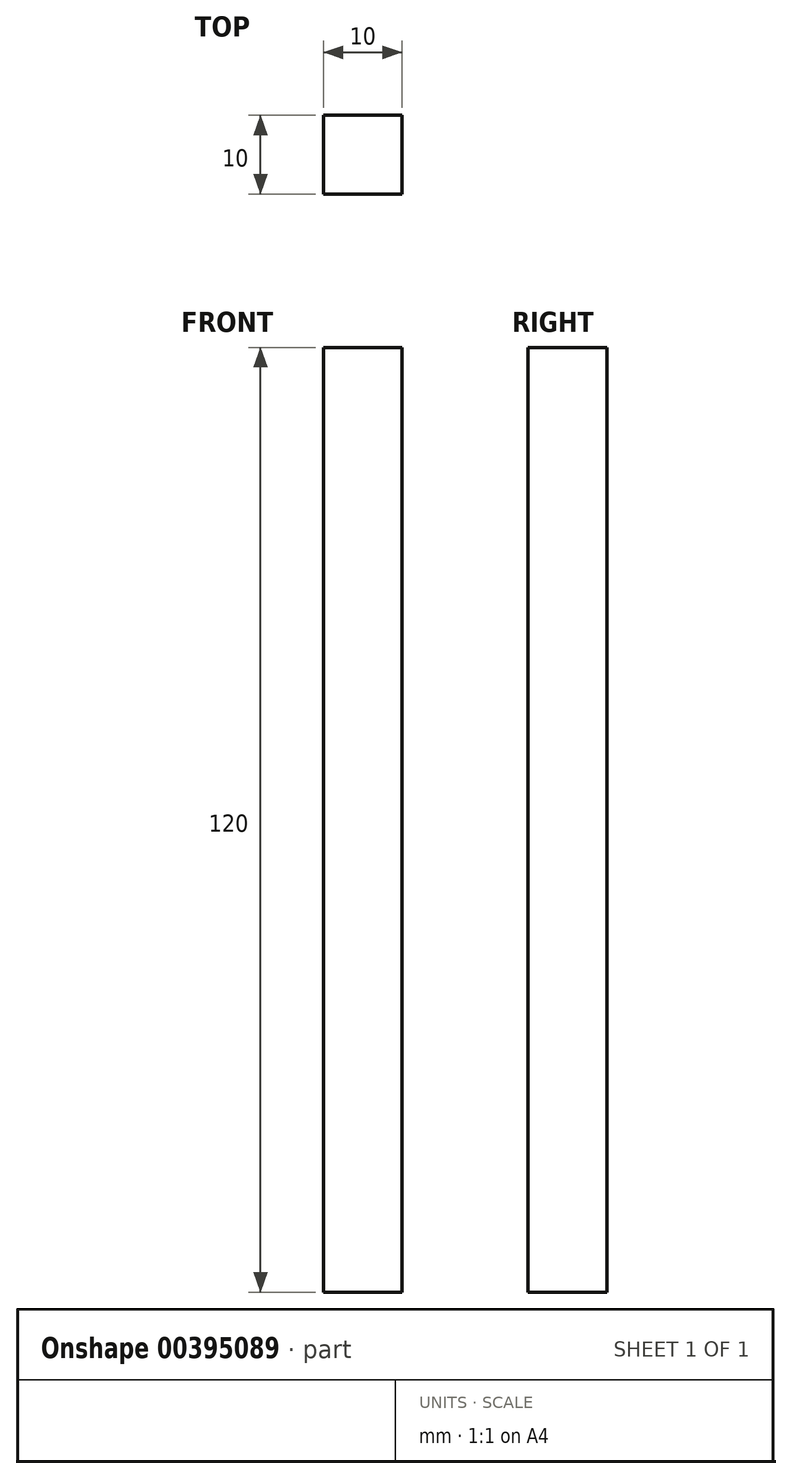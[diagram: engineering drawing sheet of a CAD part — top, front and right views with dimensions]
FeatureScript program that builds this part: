
annotation { "Feature Type Name" : "Feature", "Feature Type Description" : "" }
export const myFeature = defineFeature(function(context is Context, id is Id, definition is map)
    precondition{}
    {
        {
            var Q0;
            Q0=qCreatedBy(makeId("Front.planeOp"),FACE);
            var sketch = newSketch(context, id + "F0", { "sketchPlane" : qUnion([Q0])});
            skLineSegment(sketch, "E0.bottom", {"start": v(-5, -60) * mm, "end": v(5, -60) * mm});
            skLineSegment(sketch, "E0.top", {"start": v(-5, 60) * mm, "end": v(5, 60) * mm});
            skLineSegment(sketch, "E0.left", {"start": v(-5, -60) * mm, "end": v(-5, 60) * mm});
            skLineSegment(sketch, "E0.right", {"start": v(5, -60) * mm, "end": v(5, 60) * mm});
            skPoint(sketch, "E0.middle", {"position": v(0, 0) * mm});
            skSolve(sketch);
        }
        {
            var Q0;
            Q0 = qSketchRegion(id + "F0", true);
            extrude(context, id + "F1", {"entities" : qUnion([Q0]), "depth" : 10 * mm});
        }
    });
